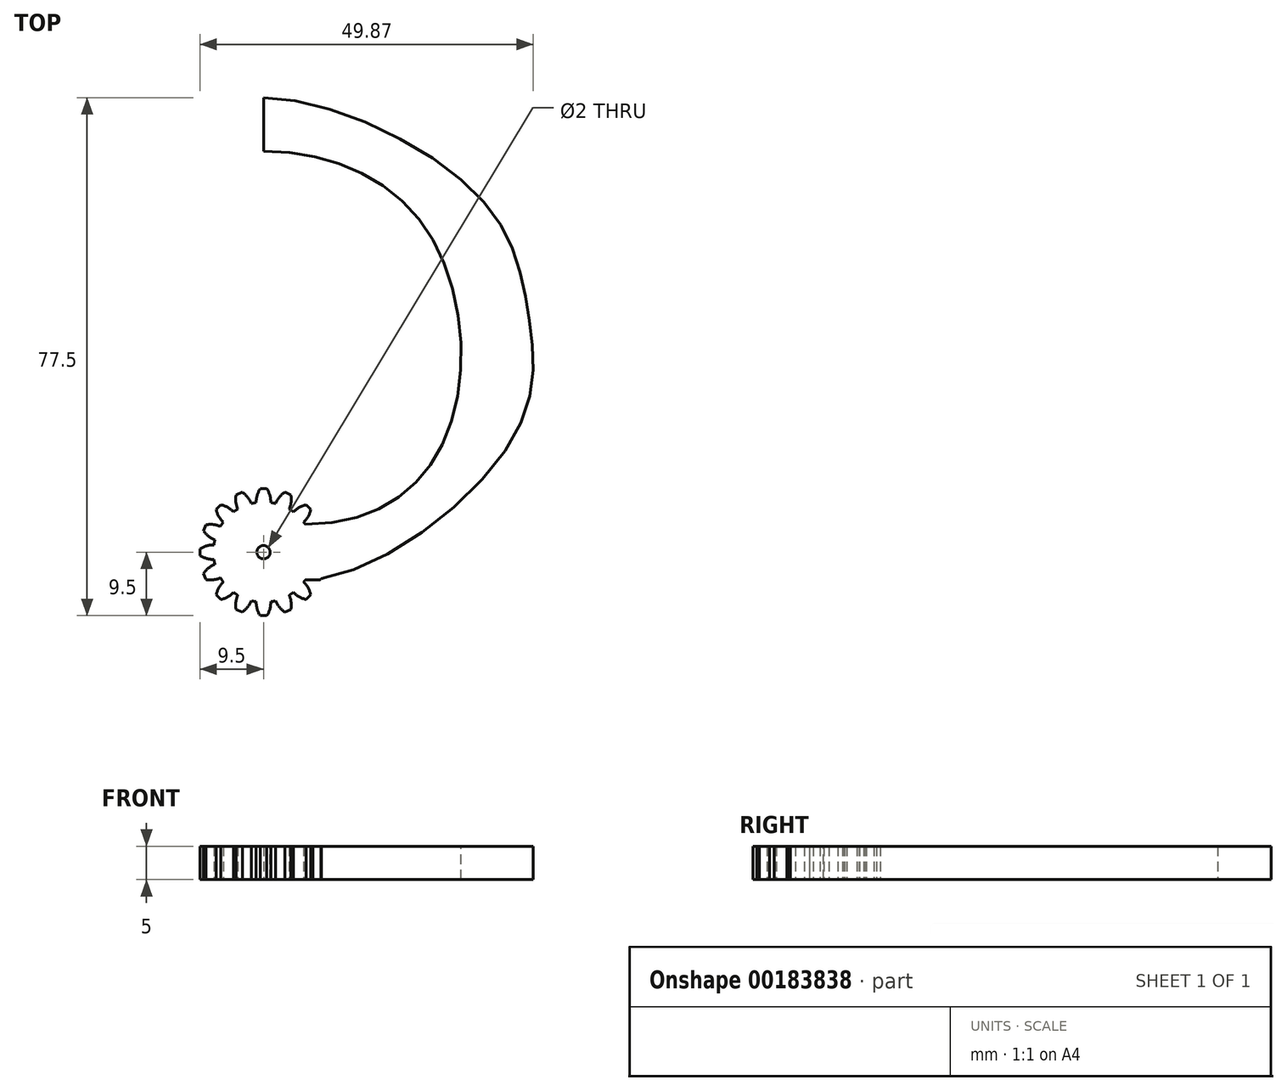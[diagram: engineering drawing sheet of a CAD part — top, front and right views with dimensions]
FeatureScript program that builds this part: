
annotation { "Feature Type Name" : "Feature", "Feature Type Description" : "" }
export const myFeature = defineFeature(function(context is Context, id is Id, definition is map)
    precondition{}
    {
        {
            var Q0;
            Q0=qCreatedBy(makeId("Top.planeOp"),FACE);
            var sketch = newSketch(context, id + "F0", { "sketchPlane" : qUnion([Q0])});
            skCircle(sketch, "E0", {"center": v(0, 0) * mm, "radius": 7.5 * mm});
            skLineSegment(sketch, "E1", {"start": v(0, 0) * mm, "end": v(0, 7.5) * mm, "construction": true});
            skLineSegment(sketch, "E2", {"start": v(0, 7.5) * mm, "end": v(0, 9.5) * mm});
            skLineSegment(sketch, "E3", {"start": v(0, 9.5) * mm, "end": v(-0.5, 9.5) * mm});
            skArc(sketch, "E4", {"start": v(-0.5, 9.5) * mm, "mid": v(-0.95, 8.5) * mm, "end": v(-1.09, 7.42) * mm});
            skLineSegment(sketch, "E5.MirrorCS", {"start": v(0, 9.5) * mm, "end": v(0.5, 9.5) * mm});
            skArc(sketch, "E6.MirrorCS", {"start": v(0.5, 9.5) * mm, "mid": v(0.95, 8.5) * mm, "end": v(1.09, 7.42) * mm});
            skArc(sketch, "E7.1.0", {"start": v(-4.1, 8.59) * mm, "mid": v(-4.13, 7.5) * mm, "end": v(-3.85, 6.44) * mm});
            skLineSegment(sketch, "E7.1.1", {"start": v(-3.64, 8.78) * mm, "end": v(-4.1, 8.59) * mm});
            skLineSegment(sketch, "E7.1.2", {"start": v(-3.64, 8.78) * mm, "end": v(-3.17, 8.97) * mm});
            skArc(sketch, "E7.1.3", {"start": v(-3.17, 8.97) * mm, "mid": v(-2.38, 8.22) * mm, "end": v(-1.83, 7.27) * mm});
            skArc(sketch, "E7.2.0", {"start": v(-7.07, 6.36) * mm, "mid": v(-6.69, 5.34) * mm, "end": v(-6.02, 4.48) * mm});
            skLineSegment(sketch, "E7.2.1", {"start": v(-6.72, 6.72) * mm, "end": v(-7.07, 6.36) * mm});
            skLineSegment(sketch, "E7.2.2", {"start": v(-6.72, 6.72) * mm, "end": v(-6.36, 7.07) * mm});
            skArc(sketch, "E7.2.3", {"start": v(-6.36, 7.07) * mm, "mid": v(-5.34, 6.69) * mm, "end": v(-4.48, 6.02) * mm});
            skArc(sketch, "E7.3.0", {"start": v(-8.97, 3.17) * mm, "mid": v(-8.22, 2.38) * mm, "end": v(-7.27, 1.83) * mm});
            skLineSegment(sketch, "E7.3.1", {"start": v(-8.78, 3.64) * mm, "end": v(-8.97, 3.17) * mm});
            skLineSegment(sketch, "E7.3.2", {"start": v(-8.78, 3.64) * mm, "end": v(-8.59, 4.1) * mm});
            skArc(sketch, "E7.3.3", {"start": v(-8.59, 4.1) * mm, "mid": v(-7.5, 4.13) * mm, "end": v(-6.44, 3.85) * mm});
            skArc(sketch, "E7.4.0", {"start": v(-9.5, -0.5) * mm, "mid": v(-8.5, -0.95) * mm, "end": v(-7.42, -1.09) * mm});
            skLineSegment(sketch, "E7.4.1", {"start": v(-9.5, 0) * mm, "end": v(-9.5, -0.5) * mm});
            skLineSegment(sketch, "E7.4.2", {"start": v(-9.5, 0) * mm, "end": v(-9.5, 0.5) * mm});
            skArc(sketch, "E7.4.3", {"start": v(-9.5, 0.5) * mm, "mid": v(-8.5, 0.95) * mm, "end": v(-7.42, 1.09) * mm});
            skArc(sketch, "E7.5.0", {"start": v(-8.59, -4.1) * mm, "mid": v(-7.5, -4.13) * mm, "end": v(-6.44, -3.85) * mm});
            skLineSegment(sketch, "E7.5.1", {"start": v(-8.78, -3.64) * mm, "end": v(-8.59, -4.1) * mm});
            skLineSegment(sketch, "E7.5.2", {"start": v(-8.78, -3.64) * mm, "end": v(-8.97, -3.17) * mm});
            skArc(sketch, "E7.5.3", {"start": v(-8.97, -3.17) * mm, "mid": v(-8.22, -2.38) * mm, "end": v(-7.27, -1.83) * mm});
            skArc(sketch, "E7.6.0", {"start": v(-6.36, -7.07) * mm, "mid": v(-5.34, -6.69) * mm, "end": v(-4.48, -6.02) * mm});
            skLineSegment(sketch, "E7.6.1", {"start": v(-6.72, -6.72) * mm, "end": v(-6.36, -7.07) * mm});
            skLineSegment(sketch, "E7.6.2", {"start": v(-6.72, -6.72) * mm, "end": v(-7.07, -6.36) * mm});
            skArc(sketch, "E7.6.3", {"start": v(-7.07, -6.36) * mm, "mid": v(-6.69, -5.34) * mm, "end": v(-6.02, -4.48) * mm});
            skArc(sketch, "E7.7.0", {"start": v(-3.17, -8.97) * mm, "mid": v(-2.38, -8.22) * mm, "end": v(-1.83, -7.27) * mm});
            skLineSegment(sketch, "E7.7.1", {"start": v(-3.64, -8.78) * mm, "end": v(-3.17, -8.97) * mm});
            skLineSegment(sketch, "E7.7.2", {"start": v(-3.64, -8.78) * mm, "end": v(-4.1, -8.59) * mm});
            skArc(sketch, "E7.7.3", {"start": v(-4.1, -8.59) * mm, "mid": v(-4.13, -7.5) * mm, "end": v(-3.85, -6.44) * mm});
            skArc(sketch, "E7.8.0", {"start": v(0.5, -9.5) * mm, "mid": v(0.95, -8.5) * mm, "end": v(1.09, -7.42) * mm});
            skLineSegment(sketch, "E7.8.1", {"start": v(0, -9.5) * mm, "end": v(0.5, -9.5) * mm});
            skLineSegment(sketch, "E7.8.2", {"start": v(0, -9.5) * mm, "end": v(-0.5, -9.5) * mm});
            skArc(sketch, "E7.8.3", {"start": v(-0.5, -9.5) * mm, "mid": v(-0.95, -8.5) * mm, "end": v(-1.09, -7.42) * mm});
            skArc(sketch, "E7.9.0", {"start": v(4.1, -8.59) * mm, "mid": v(4.13, -7.5) * mm, "end": v(3.85, -6.44) * mm});
            skLineSegment(sketch, "E7.9.1", {"start": v(3.64, -8.78) * mm, "end": v(4.1, -8.59) * mm});
            skLineSegment(sketch, "E7.9.2", {"start": v(3.64, -8.78) * mm, "end": v(3.17, -8.97) * mm});
            skArc(sketch, "E7.9.3", {"start": v(3.17, -8.97) * mm, "mid": v(2.38, -8.22) * mm, "end": v(1.83, -7.27) * mm});
            skArc(sketch, "E7.10.0", {"start": v(7.07, -6.36) * mm, "mid": v(6.69, -5.34) * mm, "end": v(6.02, -4.48) * mm});
            skLineSegment(sketch, "E7.10.1", {"start": v(6.72, -6.72) * mm, "end": v(7.07, -6.36) * mm});
            skLineSegment(sketch, "E7.10.2", {"start": v(6.72, -6.72) * mm, "end": v(6.36, -7.07) * mm});
            skArc(sketch, "E7.10.3", {"start": v(6.36, -7.07) * mm, "mid": v(5.34, -6.69) * mm, "end": v(4.48, -6.02) * mm});
            skArc(sketch, "E7.11.0", {"start": v(8.97, -3.17) * mm, "mid": v(8.22, -2.38) * mm, "end": v(7.27, -1.83) * mm});
            skLineSegment(sketch, "E7.11.1", {"start": v(8.78, -3.64) * mm, "end": v(8.97, -3.17) * mm});
            skLineSegment(sketch, "E7.11.2", {"start": v(8.78, -3.64) * mm, "end": v(8.59, -4.1) * mm});
            skArc(sketch, "E7.11.3", {"start": v(8.59, -4.1) * mm, "mid": v(7.5, -4.13) * mm, "end": v(6.44, -3.85) * mm});
            skArc(sketch, "E7.12.0", {"start": v(9.5, 0.5) * mm, "mid": v(8.5, 0.95) * mm, "end": v(7.42, 1.09) * mm});
            skLineSegment(sketch, "E7.12.1", {"start": v(9.5, 0) * mm, "end": v(9.5, 0.5) * mm});
            skLineSegment(sketch, "E7.12.2", {"start": v(9.5, 0) * mm, "end": v(9.5, -0.5) * mm});
            skArc(sketch, "E7.12.3", {"start": v(9.5, -0.5) * mm, "mid": v(8.5, -0.95) * mm, "end": v(7.42, -1.09) * mm});
            skArc(sketch, "E7.13.0", {"start": v(8.59, 4.1) * mm, "mid": v(7.5, 4.13) * mm, "end": v(6.44, 3.85) * mm});
            skLineSegment(sketch, "E7.13.1", {"start": v(8.78, 3.64) * mm, "end": v(8.59, 4.1) * mm});
            skLineSegment(sketch, "E7.13.2", {"start": v(8.78, 3.64) * mm, "end": v(8.97, 3.17) * mm});
            skArc(sketch, "E7.13.3", {"start": v(8.97, 3.17) * mm, "mid": v(8.22, 2.38) * mm, "end": v(7.27, 1.83) * mm});
            skArc(sketch, "E7.14.0", {"start": v(6.36, 7.07) * mm, "mid": v(5.34, 6.69) * mm, "end": v(4.48, 6.02) * mm});
            skLineSegment(sketch, "E7.14.1", {"start": v(6.72, 6.72) * mm, "end": v(6.36, 7.07) * mm});
            skLineSegment(sketch, "E7.14.2", {"start": v(6.72, 6.72) * mm, "end": v(7.07, 6.36) * mm});
            skArc(sketch, "E7.14.3", {"start": v(7.07, 6.36) * mm, "mid": v(6.69, 5.34) * mm, "end": v(6.02, 4.48) * mm});
            skArc(sketch, "E7.15.0", {"start": v(3.17, 8.97) * mm, "mid": v(2.38, 8.22) * mm, "end": v(1.83, 7.27) * mm});
            skLineSegment(sketch, "E7.15.1", {"start": v(3.64, 8.78) * mm, "end": v(3.17, 8.97) * mm});
            skLineSegment(sketch, "E7.15.2", {"start": v(3.64, 8.78) * mm, "end": v(4.1, 8.59) * mm});
            skArc(sketch, "E7.15.3", {"start": v(4.1, 8.59) * mm, "mid": v(4.13, 7.5) * mm, "end": v(3.85, 6.44) * mm});
            skSolve(sketch);
        }
        {
            var Q0;
            Q0=qSketchRegion(id+"F0",true);
            extrude(context, id + "F1", {"entities" : qUnion([Q0]), "depth" : 5 * mm});
        }
        {
            var Q0;
            Q0=makeQuery(id+"F1.opExtrude","CAP_FACE",FACE,{"disambiguationData":[OSD([sQuery(id+"F0.wireOp",EDGE,"E0"),sQuery(id+"F0.wireOp",EDGE,"E3"),sQuery(id+"F0.wireOp",EDGE,"E4"),sQuery(id+"F0.wireOp",EDGE,"E5.MirrorCS"),sQuery(id+"F0.wireOp",EDGE,"E6.MirrorCS"),sQuery(id+"F0.wireOp",EDGE,"E7.1.0"),sQuery(id+"F0.wireOp",EDGE,"E7.1.1"),sQuery(id+"F0.wireOp",EDGE,"E7.1.2"),sQuery(id+"F0.wireOp",EDGE,"E7.1.3"),sQuery(id+"F0.wireOp",EDGE,"E7.2.0"),sQuery(id+"F0.wireOp",EDGE,"E7.2.1"),sQuery(id+"F0.wireOp",EDGE,"E7.2.2"),sQuery(id+"F0.wireOp",EDGE,"E7.2.3"),sQuery(id+"F0.wireOp",EDGE,"E7.3.0"),sQuery(id+"F0.wireOp",EDGE,"E7.3.1"),sQuery(id+"F0.wireOp",EDGE,"E7.3.2"),sQuery(id+"F0.wireOp",EDGE,"E7.3.3"),sQuery(id+"F0.wireOp",EDGE,"E7.4.0"),sQuery(id+"F0.wireOp",EDGE,"E7.4.1"),sQuery(id+"F0.wireOp",EDGE,"E7.4.2"),sQuery(id+"F0.wireOp",EDGE,"E7.4.3"),sQuery(id+"F0.wireOp",EDGE,"E7.5.0"),sQuery(id+"F0.wireOp",EDGE,"E7.5.1"),sQuery(id+"F0.wireOp",EDGE,"E7.5.2"),sQuery(id+"F0.wireOp",EDGE,"E7.5.3"),sQuery(id+"F0.wireOp",EDGE,"E7.6.0"),sQuery(id+"F0.wireOp",EDGE,"E7.6.1"),sQuery(id+"F0.wireOp",EDGE,"E7.6.2"),sQuery(id+"F0.wireOp",EDGE,"E7.6.3"),sQuery(id+"F0.wireOp",EDGE,"E7.7.0"),sQuery(id+"F0.wireOp",EDGE,"E7.7.1"),sQuery(id+"F0.wireOp",EDGE,"E7.7.2"),sQuery(id+"F0.wireOp",EDGE,"E7.7.3"),sQuery(id+"F0.wireOp",EDGE,"E7.8.0"),sQuery(id+"F0.wireOp",EDGE,"E7.8.1"),sQuery(id+"F0.wireOp",EDGE,"E7.8.2"),sQuery(id+"F0.wireOp",EDGE,"E7.8.3"),sQuery(id+"F0.wireOp",EDGE,"E7.9.0"),sQuery(id+"F0.wireOp",EDGE,"E7.9.1"),sQuery(id+"F0.wireOp",EDGE,"E7.9.2"),sQuery(id+"F0.wireOp",EDGE,"E7.9.3"),sQuery(id+"F0.wireOp",EDGE,"E7.10.0"),sQuery(id+"F0.wireOp",EDGE,"E7.10.1"),sQuery(id+"F0.wireOp",EDGE,"E7.10.2"),sQuery(id+"F0.wireOp",EDGE,"E7.10.3"),sQuery(id+"F0.wireOp",EDGE,"E7.11.0"),sQuery(id+"F0.wireOp",EDGE,"E7.11.1"),sQuery(id+"F0.wireOp",EDGE,"E7.11.2"),sQuery(id+"F0.wireOp",EDGE,"E7.11.3"),sQuery(id+"F0.wireOp",EDGE,"E7.12.0"),sQuery(id+"F0.wireOp",EDGE,"E7.12.1"),sQuery(id+"F0.wireOp",EDGE,"E7.12.2"),sQuery(id+"F0.wireOp",EDGE,"E7.12.3"),sQuery(id+"F0.wireOp",EDGE,"E7.13.0"),sQuery(id+"F0.wireOp",EDGE,"E7.13.1"),sQuery(id+"F0.wireOp",EDGE,"E7.13.2"),sQuery(id+"F0.wireOp",EDGE,"E7.13.3"),sQuery(id+"F0.wireOp",EDGE,"E7.14.0"),sQuery(id+"F0.wireOp",EDGE,"E7.14.1"),sQuery(id+"F0.wireOp",EDGE,"E7.14.2"),sQuery(id+"F0.wireOp",EDGE,"E7.14.3"),sQuery(id+"F0.wireOp",EDGE,"E7.15.0"),sQuery(id+"F0.wireOp",EDGE,"E7.15.1"),sQuery(id+"F0.wireOp",EDGE,"E7.15.2"),sQuery(id+"F0.wireOp",EDGE,"E7.15.3")])],"isStart":false});
            var sketch = newSketch(context, id + "F2", { "sketchPlane" : qUnion([Q0])});
            skCircle(sketch, "E8", {"center": v(0, 0) * mm, "radius": 1 * mm});
            skSolve(sketch);
        }
        {
            var Q0;
            Q0=qSketchRegion(id+"F2",true);
            extrude(context, id + "F3", {"entities" : qUnion([Q0]), "operationType" : NewBodyOperationType.REMOVE, "endBound" : BoundingType.THROUGH_ALL, "oppositeDirection" : true, "depth" : 25 * mm});
        }
        {
            var Q0;
            Q0=qCreatedBy(makeId("Top.planeOp"),FACE);
            var sketch = newSketch(context, id + "F4", { "sketchPlane" : qUnion([Q0])});
            skFitSpline(sketch, "E9", {"points": [v(0, 60) * mm, v(24.67, 47.84) * mm, v(27.08, 16.8) * mm, v(6.24, 4.17) * mm], "startDerivative": vector(90.17, 0) * mm, "endDerivative": vector(-95.78, 0) * mm});
            skFitSpline(sketch, "E10", {"points": [v(0, 68) * mm, v(32.17, 53.3) * mm, v(39.6, 35.97) * mm, v(37.2, 16.8) * mm, v(6.24, -4.17) * mm], "startDerivative": vector(104.92, 0) * mm, "endDerivative": vector(-102.04, 0) * mm});
            skLineSegment(sketch, "E11", {"start": v(6.24, 4.17) * mm, "end": v(6.24, -4.17) * mm});
            skLineSegment(sketch, "E12", {"start": v(0, 68) * mm, "end": v(0, 60) * mm});
            skSolve(sketch);
        }
        {
            var Q0;
            Q0 = qSketchRegion(id + "F4", true);
            var Q1;
            Q1=makeQuery(id+"F1.opExtrude","CAP_FACE",FACE,{"disambiguationData":[OSD([sQuery(id+"F0.wireOp",EDGE,"E0"),sQuery(id+"F0.wireOp",EDGE,"E3"),sQuery(id+"F0.wireOp",EDGE,"E4"),sQuery(id+"F0.wireOp",EDGE,"E5.MirrorCS"),sQuery(id+"F0.wireOp",EDGE,"E6.MirrorCS"),sQuery(id+"F0.wireOp",EDGE,"E7.1.0"),sQuery(id+"F0.wireOp",EDGE,"E7.1.1"),sQuery(id+"F0.wireOp",EDGE,"E7.1.2"),sQuery(id+"F0.wireOp",EDGE,"E7.1.3"),sQuery(id+"F0.wireOp",EDGE,"E7.2.0"),sQuery(id+"F0.wireOp",EDGE,"E7.2.1"),sQuery(id+"F0.wireOp",EDGE,"E7.2.2"),sQuery(id+"F0.wireOp",EDGE,"E7.2.3"),sQuery(id+"F0.wireOp",EDGE,"E7.3.0"),sQuery(id+"F0.wireOp",EDGE,"E7.3.1"),sQuery(id+"F0.wireOp",EDGE,"E7.3.2"),sQuery(id+"F0.wireOp",EDGE,"E7.3.3"),sQuery(id+"F0.wireOp",EDGE,"E7.4.0"),sQuery(id+"F0.wireOp",EDGE,"E7.4.1"),sQuery(id+"F0.wireOp",EDGE,"E7.4.2"),sQuery(id+"F0.wireOp",EDGE,"E7.4.3"),sQuery(id+"F0.wireOp",EDGE,"E7.5.0"),sQuery(id+"F0.wireOp",EDGE,"E7.5.1"),sQuery(id+"F0.wireOp",EDGE,"E7.5.2"),sQuery(id+"F0.wireOp",EDGE,"E7.5.3"),sQuery(id+"F0.wireOp",EDGE,"E7.6.0"),sQuery(id+"F0.wireOp",EDGE,"E7.6.1"),sQuery(id+"F0.wireOp",EDGE,"E7.6.2"),sQuery(id+"F0.wireOp",EDGE,"E7.6.3"),sQuery(id+"F0.wireOp",EDGE,"E7.7.0"),sQuery(id+"F0.wireOp",EDGE,"E7.7.1"),sQuery(id+"F0.wireOp",EDGE,"E7.7.2"),sQuery(id+"F0.wireOp",EDGE,"E7.7.3"),sQuery(id+"F0.wireOp",EDGE,"E7.8.0"),sQuery(id+"F0.wireOp",EDGE,"E7.8.1"),sQuery(id+"F0.wireOp",EDGE,"E7.8.2"),sQuery(id+"F0.wireOp",EDGE,"E7.8.3"),sQuery(id+"F0.wireOp",EDGE,"E7.9.0"),sQuery(id+"F0.wireOp",EDGE,"E7.9.1"),sQuery(id+"F0.wireOp",EDGE,"E7.9.2"),sQuery(id+"F0.wireOp",EDGE,"E7.9.3"),sQuery(id+"F0.wireOp",EDGE,"E7.10.0"),sQuery(id+"F0.wireOp",EDGE,"E7.10.1"),sQuery(id+"F0.wireOp",EDGE,"E7.10.2"),sQuery(id+"F0.wireOp",EDGE,"E7.10.3"),sQuery(id+"F0.wireOp",EDGE,"E7.11.0"),sQuery(id+"F0.wireOp",EDGE,"E7.11.1"),sQuery(id+"F0.wireOp",EDGE,"E7.11.2"),sQuery(id+"F0.wireOp",EDGE,"E7.11.3"),sQuery(id+"F0.wireOp",EDGE,"E7.12.0"),sQuery(id+"F0.wireOp",EDGE,"E7.12.1"),sQuery(id+"F0.wireOp",EDGE,"E7.12.2"),sQuery(id+"F0.wireOp",EDGE,"E7.12.3"),sQuery(id+"F0.wireOp",EDGE,"E7.13.0"),sQuery(id+"F0.wireOp",EDGE,"E7.13.1"),sQuery(id+"F0.wireOp",EDGE,"E7.13.2"),sQuery(id+"F0.wireOp",EDGE,"E7.13.3"),sQuery(id+"F0.wireOp",EDGE,"E7.14.0"),sQuery(id+"F0.wireOp",EDGE,"E7.14.1"),sQuery(id+"F0.wireOp",EDGE,"E7.14.2"),sQuery(id+"F0.wireOp",EDGE,"E7.14.3"),sQuery(id+"F0.wireOp",EDGE,"E7.15.0"),sQuery(id+"F0.wireOp",EDGE,"E7.15.1"),sQuery(id+"F0.wireOp",EDGE,"E7.15.2"),sQuery(id+"F0.wireOp",EDGE,"E7.15.3")])],"isStart":false});
            extrude(context, id + "F5", {"entities" : qUnion([Q0]), "operationType" : NewBodyOperationType.ADD, "endBound" : BoundingType.UP_TO_SURFACE, "endBoundEntityFace" : qUnion([Q1]), "depth" : 25 * mm});
        }
    });
